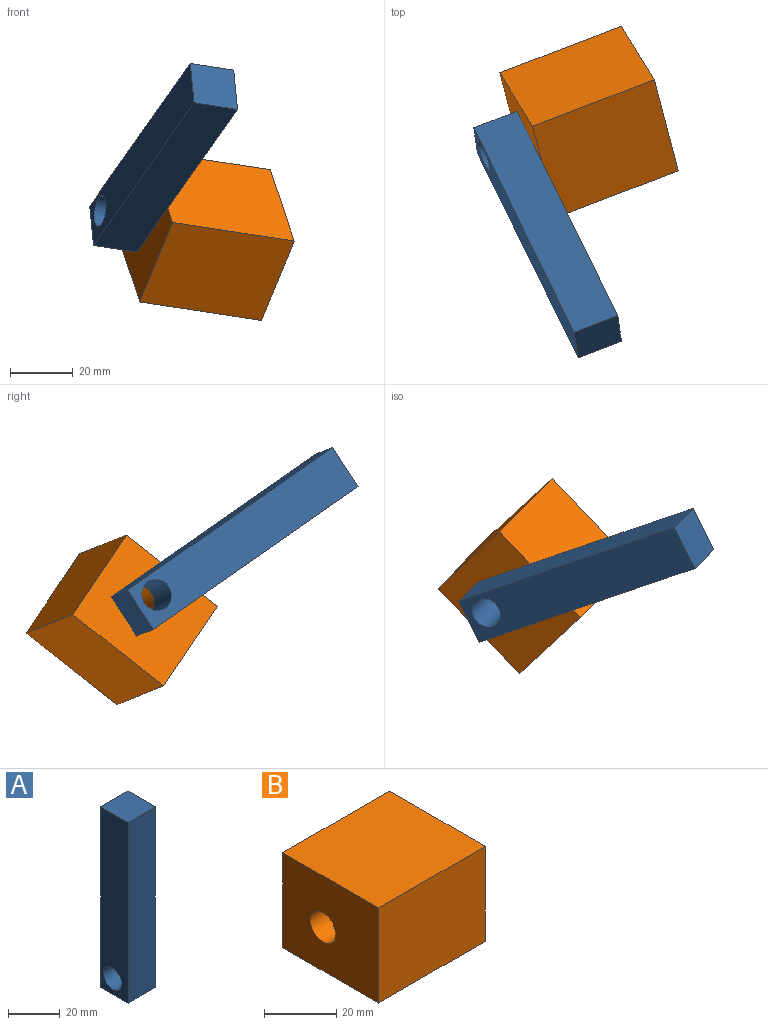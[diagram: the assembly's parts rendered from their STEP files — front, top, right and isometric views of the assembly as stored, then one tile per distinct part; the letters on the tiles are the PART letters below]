
ASSEMBLY  parts=2 mates=1
PART A: 7 faces, bbox 15x15x85.7 mm
  f0: plane 85.7x15mm, normal (1,0,0), area 1207mm2, adj f1,f3,f4,f5,f6
  f1: plane 85.7x15mm, normal (0,1,0), area 1285.5mm2, adj f0,f2,f4,f5
  f2: plane 85.7x15mm, normal (-1,0,0), area 1207mm2, adj f1,f3,f4,f5,f6
  f3: plane 85.7x15mm, normal (0,-1,0), area 1285.5mm2, adj f0,f2,f4,f5
  f4: plane 15x15mm, normal (0,0,1), area 225mm2, adj f0,f1,f2,f3
  f5: plane 15x15mm, normal (0,0,-1), area 225mm2, adj f0,f1,f2,f3
  f6: cylinder r=5mm len=15mm, axis (1,0,0), area 471.2mm2, adj f0,f2
PART B: 7 faces, bbox 42x37.6x32.3 mm
  f0: plane 37.63x32.3mm, normal (-1,0,0), area 1137mm2, adj f1,f3,f4,f5,f6
  f1: plane 41.95x32.3mm, normal (0,-1,0), area 1355.1mm2, adj f0,f2,f4,f5
  f2: plane 37.63x32.3mm, normal (1,0,0), area 1137mm2, adj f1,f3,f4,f5,f6
  f3: plane 41.95x32.3mm, normal (0,1,0), area 1355.1mm2, adj f0,f2,f4,f5
  f4: plane 41.95x37.63mm, normal (0,0,1), area 1578.8mm2, adj f0,f1,f2,f3
  f5: plane 41.95x37.63mm, normal (0,0,-1), area 1578.8mm2, adj f0,f1,f2,f3
  f6: cylinder r=5mm len=41.95mm, axis (1,0,0), area 1318mm2, adj f0,f2
PLACE A rot(axis=(0.92,0.3,0.25),60.1deg) t=(0.69,103.62,-53.65)mm
PLACE B rot(axis=(0.15,-0.94,-0.31),165.7deg) t=(43.13,121.78,-27.41)mm
MATE revolute B.f6 <-> A.f6  axis (-0.92,-0.35,0.14) through (2.76,102.6,-42.68)mm
